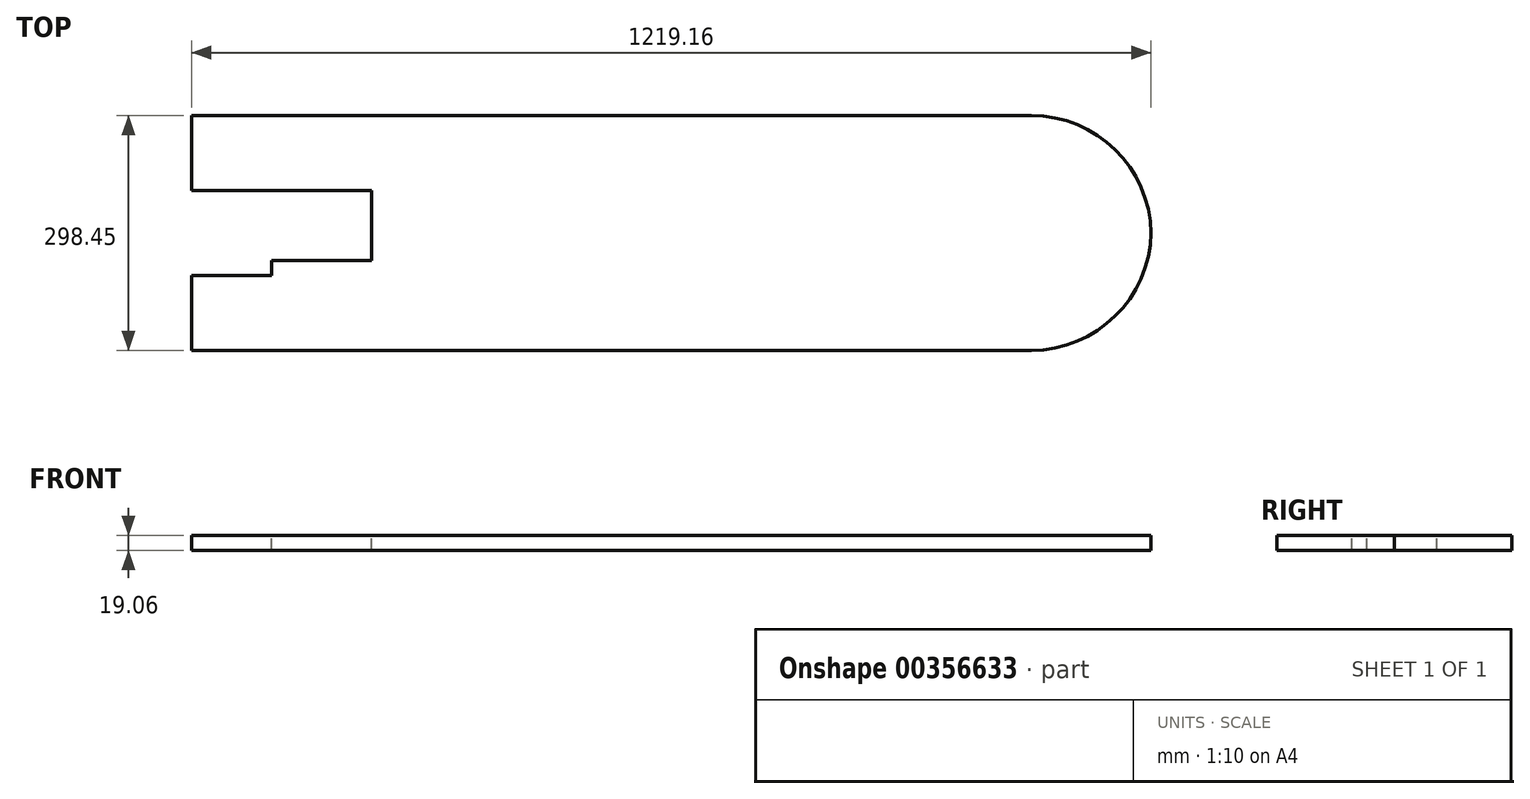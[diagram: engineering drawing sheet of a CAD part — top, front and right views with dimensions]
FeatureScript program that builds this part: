
annotation { "Feature Type Name" : "Feature", "Feature Type Description" : "" }
export const myFeature = defineFeature(function(context is Context, id is Id, definition is map)
    precondition{}
    {
        {
            var Q0;
            Q0=qCreatedBy(makeId("Top.planeOp"),FACE);
            var sketch = newSketch(context, id + "F0", { "sketchPlane" : qUnion([Q0])});
            skLineSegment(sketch, "E0", {"start": v(97.49, 41.73) * mm, "end": v(97.49, -53.52) * mm});
            skLineSegment(sketch, "E1", {"start": v(97.49, -53.52) * mm, "end": v(326.09, -53.52) * mm});
            skLineSegment(sketch, "E2", {"start": v(326.09, -53.52) * mm, "end": v(326.09, -142.42) * mm});
            skLineSegment(sketch, "E3", {"start": v(326.09, -142.42) * mm, "end": v(199.09, -142.42) * mm});
            skLineSegment(sketch, "E4", {"start": v(199.09, -142.42) * mm, "end": v(199.09, -161.47) * mm});
            skLineSegment(sketch, "E5", {"start": v(199.09, -161.47) * mm, "end": v(97.49, -161.47) * mm});
            skLineSegment(sketch, "E6", {"start": v(97.49, -161.47) * mm, "end": v(97.49, -256.72) * mm});
            skLineSegment(sketch, "E7", {"start": v(97.49, -256.72) * mm, "end": v(1164.29, -256.72) * mm});
            skLineSegment(sketch, "E8", {"start": v(1316.69, -110.67) * mm, "end": v(1316.69, -104.32) * mm});
            skLineSegment(sketch, "E9", {"start": v(1164.29, 41.73) * mm, "end": v(97.49, 41.73) * mm});
            skPoint(sketch, "E10.visualSharp", {"position": v(1316.69, 41.73) * mm});
            skArc(sketch, "E10.filletArc", {"start": v(1316.69, -110.67) * mm, "mid": v(1272.05, -2.9) * mm, "end": v(1164.29, 41.73) * mm});
            skPoint(sketch, "E11.visualSharp", {"position": v(1316.69, -256.72) * mm});
            skArc(sketch, "E11.filletArc", {"start": v(1164.29, -256.72) * mm, "mid": v(1272.05, -212.08) * mm, "end": v(1316.69, -104.32) * mm});
            skSolve(sketch);
        }
        {
            var Q0;
            Q0=makeQuery(id+"F0.imprint","IMPRINT",FACE,{"disambiguationData":[TD([[makeQuery(id+"F0.imprint","IMPRINT",EDGE,{"derivedFrom":sQuery(id+"F0.wireOp",EDGE,"E0")}),1.0]])]});
            extrude(context, id + "F1", {"entities" : qUnion([Q0]), "endBound" : BoundingType.SYMMETRIC, "oppositeDirection" : true, "depth" : 19.05 * mm});
        }
    });
